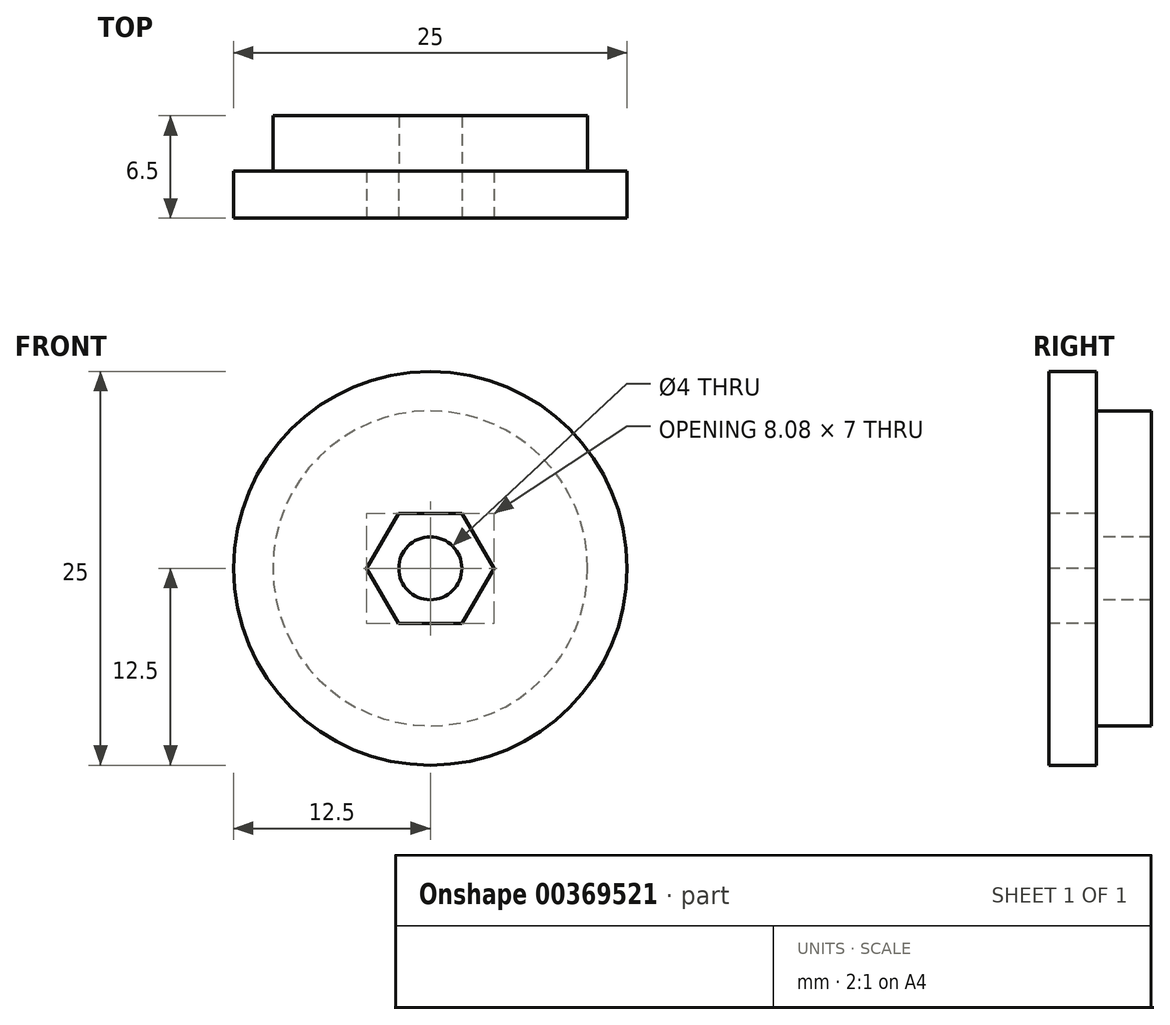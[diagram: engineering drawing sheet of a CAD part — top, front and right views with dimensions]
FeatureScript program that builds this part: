
annotation { "Feature Type Name" : "Feature", "Feature Type Description" : "" }
export const myFeature = defineFeature(function(context is Context, id is Id, definition is map)
    precondition{}
    {
        {
            var Q0;
            Q0=qCreatedBy(makeId("Front.planeOp"),FACE);
            var sketch = newSketch(context, id + "F0", { "sketchPlane" : qUnion([Q0])});
            skCircle(sketch, "E0", {"center": v(0, 0) * mm, "radius": 10 * mm});
            skSolve(sketch);
        }
        {
            var Q0;
            Q0=makeQuery(id+"F0.imprint","IMPRINT",FACE,{"disambiguationData":[TD([[makeQuery(id+"F0.imprint","IMPRINT",EDGE,{"derivedFrom":sQuery(id+"F0.wireOp",EDGE,"E0")}),1.0]])]});
            extrude(context, id + "F1", {"entities" : qUnion([Q0]), "depth" : 3.5 * mm});
        }
        {
            var Q0;
            Q0=makeQuery(id+"F1.opExtrude","CAP_FACE",FACE,{"disambiguationData":[OSD([sQuery(id+"F0.wireOp",EDGE,"E0")])],"isStart":false});
            var sketch = newSketch(context, id + "F2", { "sketchPlane" : qUnion([Q0])});
            skCircle(sketch, "E1", {"center": v(0, 0) * mm, "radius": 12.5 * mm});
            skSolve(sketch);
        }
        {
            var Q0;
            Q0=makeQuery(id+"F2.imprint","IMPRINT",FACE,{"disambiguationData":[TD([[makeQuery(id+"F2.imprint","IMPRINT",EDGE,{"derivedFrom":sQuery(id+"F2.wireOp",EDGE,"E1")}),1.0]])]});
            var Q1;
            Q1=makeQuery(id+"F2.imprint","IMPRINT",FACE,{"disambiguationData":[TD([[makeQuery(id+"F2.imprint","IMPRINT",EDGE,{"derivedFrom":makeQuery(id+"F1.opExtrude","CAP_EDGE",EDGE,{"disambiguationData":[OSD([sQuery(id+"F0.wireOp",EDGE,"E0")])],"isStart":false})}),1.0]])]});
            extrude(context, id + "F3", {"entities" : qUnion([Q0, Q1]), "depth" : 3 * mm});
        }
        {
            var Q0;
            Q0=makeQuery(id+"F3.opExtrude","CAP_FACE",FACE,{"disambiguationData":[OSD([sQuery(id+"F2.wireOp",EDGE,"E1")])],"isStart":false});
            var sketch = newSketch(context, id + "F4", { "sketchPlane" : qUnion([Q0])});
            skCircle(sketch, "E2", {"center": v(0, 0) * mm, "radius": 2 * mm});
            skSolve(sketch);
        }
        {
            var Q0;
            Q0=makeQuery(id+"F4.imprint","IMPRINT",FACE,{"disambiguationData":[TD([[makeQuery(id+"F4.imprint","IMPRINT",EDGE,{"derivedFrom":sQuery(id+"F4.wireOp",EDGE,"E2")}),1.0]])]});
            extrude(context, id + "F5", {"entities" : qUnion([Q0]), "operationType" : NewBodyOperationType.REMOVE, "oppositeDirection" : true, "depth" : 25 * mm});
        }
        {
            var Q0;
            Q0=makeQuery(id+"F3.opExtrude","CAP_FACE",FACE,{"disambiguationData":[OSD([sQuery(id+"F2.wireOp",EDGE,"E1")])],"isStart":false});
            var sketch = newSketch(context, id + "F6", { "sketchPlane" : qUnion([Q0])});
            skCircle(sketch, "E3.cCircle", {"center": v(0, 0) * mm, "radius": 3.5 * mm, "construction": true});
            skLineSegment(sketch, "E3.0", {"start": v(-2.02, 3.5) * mm, "end": v(2.02, 3.5) * mm});
            skLineSegment(sketch, "E3.1", {"start": v(2.02, 3.5) * mm, "end": v(4.04, 0) * mm});
            skLineSegment(sketch, "E3.2", {"start": v(4.04, 0) * mm, "end": v(2.02, -3.5) * mm});
            skLineSegment(sketch, "E3.3", {"start": v(2.02, -3.5) * mm, "end": v(-2.02, -3.5) * mm});
            skLineSegment(sketch, "E3.4", {"start": v(-2.02, -3.5) * mm, "end": v(-4.04, 0) * mm});
            skLineSegment(sketch, "E3.5", {"start": v(-4.04, 0) * mm, "end": v(-2.02, 3.5) * mm});
            skPoint(sketch, "E3.0.midPoint", {"position": v(0, 3.5) * mm});
            skSolve(sketch);
        }
        {
            var Q0;
            Q0=makeQuery(id+"F6.imprint","IMPRINT",FACE,{"disambiguationData":[TD([[makeQuery(id+"F6.imprint","IMPRINT",EDGE,{"derivedFrom":sQuery(id+"F6.wireOp",EDGE,"E3.0")}),-1.0]])]});
            extrude(context, id + "F7", {"entities" : qUnion([Q0]), "operationType" : NewBodyOperationType.REMOVE, "oppositeDirection" : true, "depth" : 3 * mm});
        }
    });
